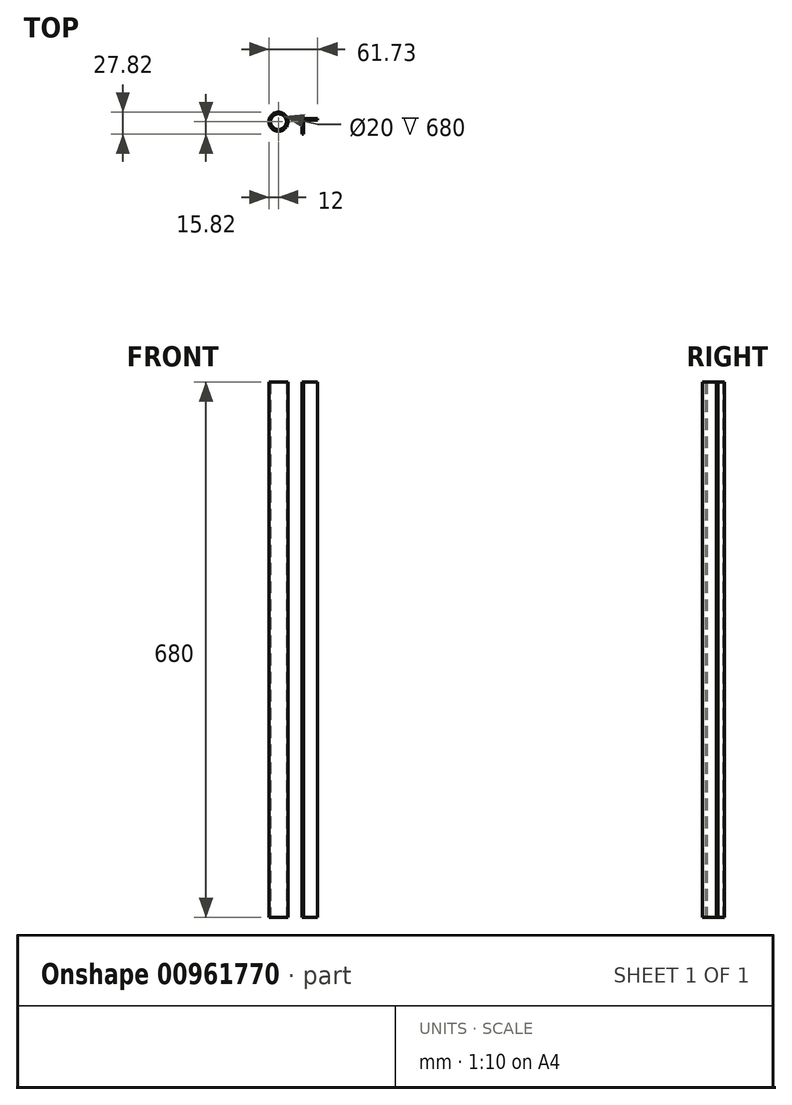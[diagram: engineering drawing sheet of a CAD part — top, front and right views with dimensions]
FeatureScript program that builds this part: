
annotation { "Feature Type Name" : "Feature", "Feature Type Description" : "" }
export const myFeature = defineFeature(function(context is Context, id is Id, definition is map)
    precondition{}
    {
        {
            var Q0;
            Q0=qCreatedBy(makeId("Top.planeOp"),FACE);
            var sketch = newSketch(context, id + "F0", { "sketchPlane" : qUnion([Q0])});
            skCircle(sketch, "E0", {"center": v(0, 0) * mm, "radius": 12 * mm});
            skLineSegment(sketch, "E1.bottom", {"start": v(29.73, 4.18) * mm, "end": v(31.73, 4.18) * mm});
            skLineSegment(sketch, "E1.top", {"start": v(29.73, -15.82) * mm, "end": v(31.73, -15.82) * mm});
            skLineSegment(sketch, "E1.left", {"start": v(29.73, 4.18) * mm, "end": v(29.73, -15.82) * mm});
            skLineSegment(sketch, "E1.right", {"start": v(31.73, 2.18) * mm, "end": v(31.73, -15.82) * mm});
            skLineSegment(sketch, "E2.bottom", {"start": v(29.73, 4.18) * mm, "end": v(49.73, 4.18) * mm});
            skLineSegment(sketch, "E2.top", {"start": v(31.73, 2.18) * mm, "end": v(49.73, 2.18) * mm});
            skLineSegment(sketch, "E2.left", {"start": v(29.73, 4.18) * mm, "end": v(29.73, 2.18) * mm});
            skLineSegment(sketch, "E2.right", {"start": v(49.73, 4.18) * mm, "end": v(49.73, 2.18) * mm});
            skSolve(sketch);
        }
        {
            var Q0;
            Q0=makeQuery(id+"F0.imprint","IMPRINT",FACE,{"disambiguationData":[TD([[makeQuery(id+"F0.imprint","IMPRINT",EDGE,{"derivedFrom":sQuery(id+"F0.wireOp",EDGE,"E0")}),1.0]])]});
            var Q1;
            Q1=makeQuery(id+"F0.imprint","IMPRINT",FACE,{"disambiguationData":[TD([[makeQuery(id+"F0.imprint","IMPRINT",EDGE,{"derivedFrom":sQuery(id+"F0.wireOp",EDGE,"E1.top")}),1.0]])]});
            extrude(context, id + "F1", {"entities" : qUnion([Q0, Q1]), "depth" : 680 * mm, "offsetDistance" : 25 * mm});
        }
        {
            var Q0;
            Q0=sQuery(id+"F0.wireOp",VERTEX,"E0.center");
            var Q1;
            Q1=makeQuery(id+"F1.opExtrude","SWEPT_BODY",BODY,{"disambiguationData":[OSD([sQuery(id+"F0.wireOp",EDGE,"E0")])]});
            hole(context, id + "F2", {"style" : HoleStyle.SIMPLE, "endStyle" : HoleEndStyle.THROUGH, "oppositeDirection" : true, "holeDiameter" : 20 * mm, "majorDiameter" : 5 * mm, "isTappedThrough" : true, "tappedDepth" : 12 * mm, "tapClearance" : 3, "locations" : qUnion([Q0]), "scope" : qUnion([Q1])});
        }
    });
